FCSTD DOCUMENT  (FreeCAD 0.21R33771 (Git))
Label: HAMMOND 162F20
License: All rights reserved
LicenseURL: https://en.wikipedia.org/wiki/All_rights_reserved
objects: Sketcher::SketchObject×1, PartDesign::Body×1
note: 2 computed .brp shape members not serialized (recipe doc carries the construction recipe); baked Part::Feature solids carry a one-line shape summary decoded from their .brp

FEATURE [Sketcher::SketchObject] Sketch
  FullyConstrained = false
  MapMode = 5
  Support = -> [XY_Plane]
  expr: .Constraints.L = 1.625 * 25.4
  sketch-geometry (4):
    g0: LineSegment StartX=-18.1457 StartY=13.4002 StartZ=0 EndX=23.1293 EndY=13.4002 EndZ=0
    g1: LineSegment StartX=23.1293 StartY=13.4002 StartZ=0 EndX=23.1293 EndY=-3.10982 EndZ=0
    g2: LineSegment StartX=23.1293 StartY=-3.10982 StartZ=0 EndX=-18.1457 EndY=-3.10982 EndZ=0
    g3: LineSegment StartX=-18.1457 StartY=-3.10982 StartZ=0 EndX=-18.1457 EndY=13.4002 EndZ=0
  constraints (10):
    c: Coincident(g0,g1)
    c: Coincident(g1,g2)
    c: Coincident(g2,g3)
    c: Coincident(g3,g0)
    c: Horizontal(g0)
    c: Horizontal(g2)
    c: Vertical(g1)
    c: Vertical(g3)
    c: Distance(g0,g0) = 41.275  'L'
    c: Distance(g1) = 16.51  'K'
FEATURE [PartDesign::Body] Body
  Group = -> [Sketch]
  Origin = -> Origin
